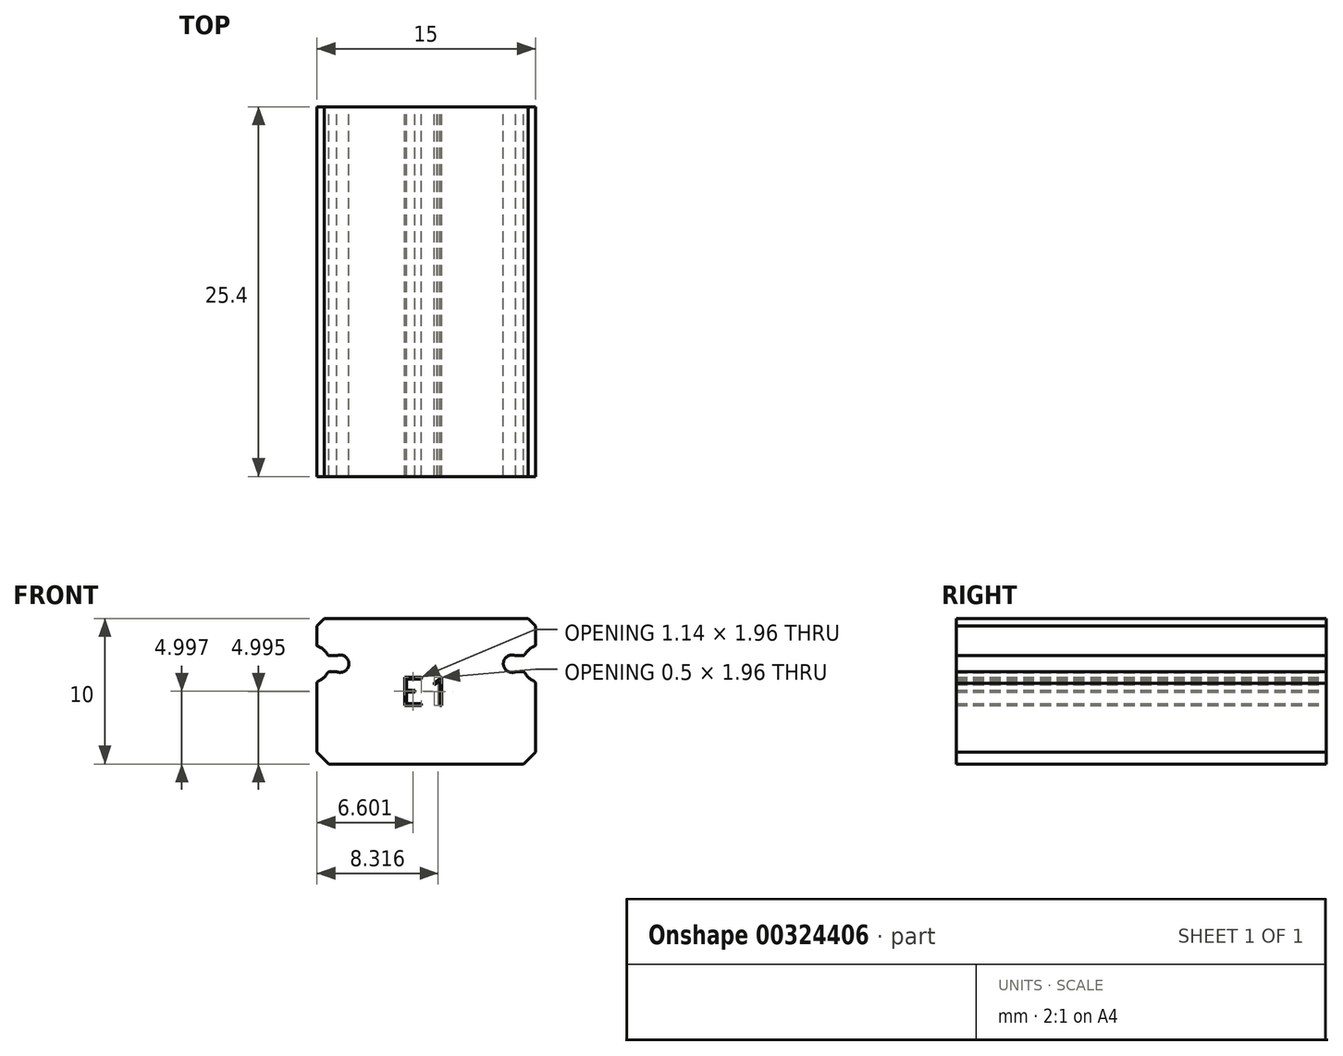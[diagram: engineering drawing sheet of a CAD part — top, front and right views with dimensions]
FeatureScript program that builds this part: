
annotation { "Feature Type Name" : "Feature", "Feature Type Description" : "" }
export const myFeature = defineFeature(function(context is Context, id is Id, definition is map)
    precondition{}
    {
        {
            var Q0;
            Q0=qCreatedBy(makeId("Front.planeOp"),FACE);
            var sketch = newSketch(context, id + "F0", { "sketchPlane" : qUnion([Q0])});
            skLineSegment(sketch, "E0", {"start": v(-6.7, -8) * mm, "end": v(-7.5, -7.2) * mm});
            skLineSegment(sketch, "E1", {"start": v(7.5, 1.5) * mm, "end": v(7, 2) * mm});
            skLineSegment(sketch, "E2", {"start": v(-6.7, -8) * mm, "end": v(6.7, -8) * mm});
            skLineSegment(sketch, "E3", {"start": v(0.93, -3.99) * mm, "end": v(1.06, -3.99) * mm});
            skLineSegment(sketch, "E4", {"start": v(-1.47, -3.98) * mm, "end": v(-0.33, -3.98) * mm});
            skLineSegment(sketch, "E5", {"start": v(-1.34, -3.85) * mm, "end": v(-0.33, -3.85) * mm});
            skLineSegment(sketch, "E6", {"start": v(-1.34, -3.07) * mm, "end": v(-0.79, -3.07) * mm});
            skLineSegment(sketch, "E7", {"start": v(-1.34, -2.94) * mm, "end": v(-0.79, -2.94) * mm});
            skLineSegment(sketch, "E8", {"start": v(-1.34, -2.15) * mm, "end": v(-0.33, -2.15) * mm});
            skLineSegment(sketch, "E9", {"start": v(1.04, -2.03) * mm, "end": v(1.06, -2.03) * mm});
            skLineSegment(sketch, "E10", {"start": v(-1.47, -2.02) * mm, "end": v(-0.33, -2.02) * mm});
            skLineSegment(sketch, "E11", {"start": v(6.14, -1.66) * mm, "end": v(6.63, -1.66) * mm});
            skLineSegment(sketch, "E12", {"start": v(-6.63, -1.66) * mm, "end": v(-6.14, -1.66) * mm});
            skLineSegment(sketch, "E13", {"start": v(-6.63, -0.55) * mm, "end": v(-6.14, -0.55) * mm});
            skLineSegment(sketch, "E14", {"start": v(6.14, -0.55) * mm, "end": v(6.63, -0.55) * mm});
            skLineSegment(sketch, "E15", {"start": v(-7, 2) * mm, "end": v(7, 2) * mm});
            skLineSegment(sketch, "E16", {"start": v(0.57, -2.54) * mm, "end": v(0.78, -2.43) * mm});
            skLineSegment(sketch, "E17", {"start": v(0.57, -2.4) * mm, "end": v(0.76, -2.3) * mm});
            skLineSegment(sketch, "E18", {"start": v(0.76, -2.3) * mm, "end": v(1.04, -2.03) * mm});
            skLineSegment(sketch, "E19", {"start": v(-7.5, 1.5) * mm, "end": v(-7, 2) * mm});
            skLineSegment(sketch, "E20", {"start": v(6.7, -8) * mm, "end": v(7.5, -7.2) * mm});
            skLineSegment(sketch, "E21", {"start": v(0.78, -2.43) * mm, "end": v(0.93, -2.28) * mm});
            skLineSegment(sketch, "E22", {"start": v(-7.5, -7.2) * mm, "end": v(-7.5, -2.45) * mm});
            skLineSegment(sketch, "E23", {"start": v(-7.5, 0.16) * mm, "end": v(-7.5, 1.5) * mm});
            skLineSegment(sketch, "E24", {"start": v(-1.47, -3.98) * mm, "end": v(-1.47, -2.02) * mm});
            skLineSegment(sketch, "E25", {"start": v(-1.34, -2.94) * mm, "end": v(-1.34, -2.15) * mm});
            skLineSegment(sketch, "E26", {"start": v(-1.34, -3.85) * mm, "end": v(-1.34, -3.07) * mm});
            skLineSegment(sketch, "E27", {"start": v(-0.79, -3.07) * mm, "end": v(-0.79, -2.94) * mm});
            skLineSegment(sketch, "E28", {"start": v(-0.33, -3.98) * mm, "end": v(-0.33, -3.85) * mm});
            skLineSegment(sketch, "E29", {"start": v(-0.33, -2.15) * mm, "end": v(-0.33, -2.02) * mm});
            skLineSegment(sketch, "E30", {"start": v(0.57, -2.54) * mm, "end": v(0.57, -2.4) * mm});
            skLineSegment(sketch, "E31", {"start": v(0.93, -3.99) * mm, "end": v(0.93, -2.28) * mm});
            skLineSegment(sketch, "E32", {"start": v(1.06, -3.99) * mm, "end": v(1.06, -2.03) * mm});
            skLineSegment(sketch, "E33", {"start": v(7.5, -7.2) * mm, "end": v(7.5, -2.45) * mm});
            skLineSegment(sketch, "E34", {"start": v(7.5, 0.16) * mm, "end": v(7.5, 1.5) * mm});
            skArc(sketch, "E35", {"start": v(-6.78, -0.46) * mm, "mid": v(-7.07, -0.12) * mm, "end": v(-7.46, 0.1) * mm});
            skArc(sketch, "E36", {"start": v(-7.4, -2.3) * mm, "mid": v(-7.04, -2.07) * mm, "end": v(-6.78, -1.75) * mm});
            skArc(sketch, "E37", {"start": v(-7.5, 0.16) * mm, "mid": v(-7.49, 0.13) * mm, "end": v(-7.46, 0.1) * mm});
            skArc(sketch, "E38", {"start": v(-7.4, -2.3) * mm, "mid": v(-7.47, -2.35) * mm, "end": v(-7.5, -2.45) * mm});
            skArc(sketch, "E39", {"start": v(-6.63, -1.66) * mm, "mid": v(-6.72, -1.68) * mm, "end": v(-6.78, -1.75) * mm});
            skArc(sketch, "E40", {"start": v(-6.78, -0.46) * mm, "mid": v(-6.72, -0.53) * mm, "end": v(-6.63, -0.55) * mm});
            skArc(sketch, "E41", {"start": v(-6.14, -1.66) * mm, "mid": v(-5.3, -1.1) * mm, "end": v(-6.14, -0.55) * mm});
            skArc(sketch, "E42", {"start": v(6.14, -0.55) * mm, "mid": v(5.3, -1.1) * mm, "end": v(6.14, -1.66) * mm});
            skArc(sketch, "E43", {"start": v(6.78, -1.75) * mm, "mid": v(6.72, -1.68) * mm, "end": v(6.63, -1.66) * mm});
            skArc(sketch, "E44", {"start": v(6.63, -0.55) * mm, "mid": v(6.72, -0.53) * mm, "end": v(6.78, -0.46) * mm});
            skArc(sketch, "E45", {"start": v(7.5, -2.45) * mm, "mid": v(7.47, -2.35) * mm, "end": v(7.4, -2.3) * mm});
            skArc(sketch, "E46", {"start": v(7.46, 0.1) * mm, "mid": v(7.49, 0.13) * mm, "end": v(7.5, 0.16) * mm});
            skArc(sketch, "E47", {"start": v(7.46, 0.1) * mm, "mid": v(7.07, -0.12) * mm, "end": v(6.78, -0.46) * mm});
            skArc(sketch, "E48", {"start": v(6.78, -1.75) * mm, "mid": v(7.04, -2.07) * mm, "end": v(7.4, -2.3) * mm});
            skSolve(sketch);
        }
        {
            var Q0;
            Q0=makeQuery(id+"F0.imprint","IMPRINT",FACE,{"disambiguationData":[TD([[makeQuery(id+"F0.imprint","IMPRINT",EDGE,{"derivedFrom":sQuery(id+"F0.wireOp",EDGE,"E0")}),-1.0]])]});
            extrude(context, id + "F1", {"entities" : qUnion([Q0]), "depth" : 25.4 * mm});
        }
    });
